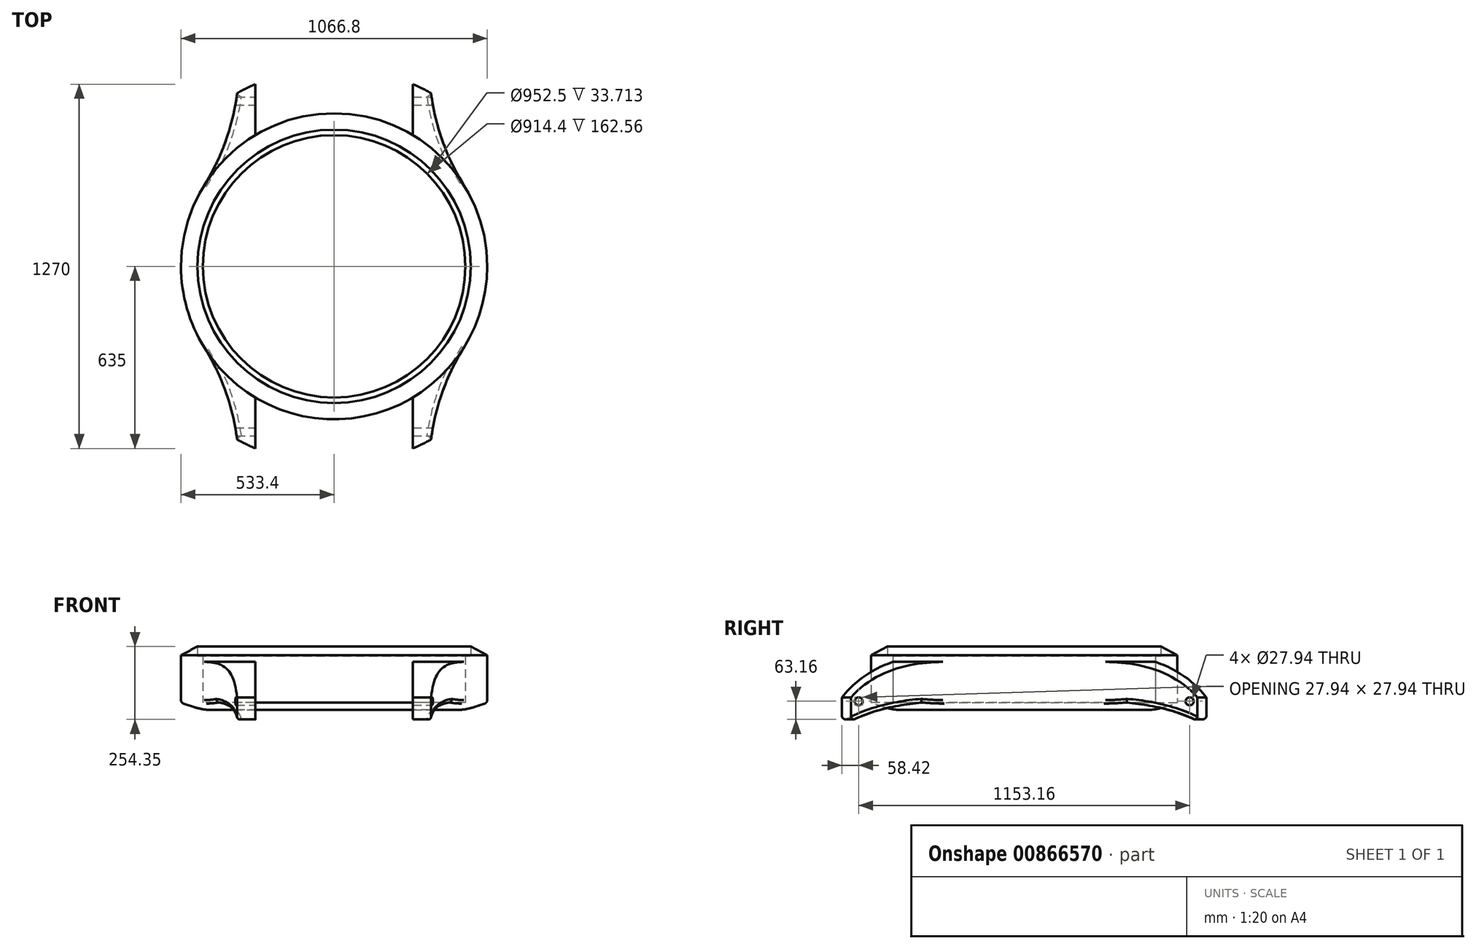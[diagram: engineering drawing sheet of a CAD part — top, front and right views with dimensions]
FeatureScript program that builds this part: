
annotation { "Feature Type Name" : "Feature", "Feature Type Description" : "" }
export const myFeature = defineFeature(function(context is Context, id is Id, definition is map)
    precondition{}
    {
        {
            var Q0;
            Q0=qCreatedBy(makeId("Top.planeOp"),FACE);
            var sketch = newSketch(context, id + "F0", { "sketchPlane" : qUnion([Q0])});
            skCircle(sketch, "E0", {"center": v(0, 0) * mm, "radius": 533.4 * mm});
            skLineSegment(sketch, "E1", {"start": v(0, 0) * mm, "end": v(533.4, 0) * mm, "construction": true});
            skLineSegment(sketch, "E2", {"start": v(0, 0) * mm, "end": v(452.35, 282.66) * mm, "construction": true});
            skLineSegment(sketch, "E3", {"start": v(452.35, 282.66) * mm, "end": v(628.97, 0) * mm, "construction": true});
            skCircle(sketch, "E4", {"center": v(0, 0) * mm, "radius": 476.25 * mm});
            skLineSegment(sketch, "E5", {"start": v(0, 0) * mm, "end": v(0, 635) * mm, "construction": true});
            skLineSegment(sketch, "E6", {"start": v(0, 635) * mm, "end": v(274.32, 635) * mm, "construction": true});
            skLineSegment(sketch, "E7", {"start": v(274.32, 635) * mm, "end": v(274.32, 457.45) * mm});
            skArc(sketch, "E8", {"start": v(337.82, 603.62) * mm, "mid": v(377.7, 436.94) * mm, "end": v(452.35, 282.66) * mm});
            skLineSegment(sketch, "E9.MirrorCS", {"start": v(-274.32, 635) * mm, "end": v(-274.32, 457.45) * mm});
            skArc(sketch, "E10.MirrorCS", {"start": v(-337.82, 603.62) * mm, "mid": v(-377.7, 436.94) * mm, "end": v(-452.35, 282.66) * mm});
            skArc(sketch, "E11.MirrorCS", {"start": v(-337.82, -603.62) * mm, "mid": v(-377.7, -436.94) * mm, "end": v(-452.35, -282.66) * mm});
            skLineSegment(sketch, "E12.MirrorCS", {"start": v(-274.32, -635) * mm, "end": v(-274.32, -457.45) * mm});
            skLineSegment(sketch, "E13.MirrorCS", {"start": v(274.32, -635) * mm, "end": v(274.32, -457.45) * mm});
            skArc(sketch, "E14.MirrorCS", {"start": v(337.82, -603.62) * mm, "mid": v(377.7, -436.94) * mm, "end": v(452.35, -282.66) * mm});
            skCircle(sketch, "E15", {"center": v(0, 0) * mm, "radius": 457.2 * mm});
            skArc(sketch, "E16", {"start": v(-337.82, -603.62) * mm, "mid": v(-306.47, -620.12) * mm, "end": v(-274.32, -635) * mm});
            skPoint(sketch, "E17.orphan", {"position": v(-331.42, 708.69) * mm});
            skPoint(sketch, "E18.MirrorCS.start.orphan", {"position": v(-274.32, 635) * mm});
            skPoint(sketch, "E19.orphan", {"position": v(331.42, 708.69) * mm});
            skPoint(sketch, "E20.MirrorCS.end.orphan", {"position": v(331.42, -708.69) * mm});
            skPoint(sketch, "E20.MirrorCS.start.orphan", {"position": v(274.32, -635) * mm});
            skPoint(sketch, "E21.orphan", {"position": v(-331.42, -708.69) * mm});
            skPoint(sketch, "E22.MirrorCS.start.orphan", {"position": v(-274.32, -635) * mm});
            skArc(sketch, "E23.trimOffspring", {"start": v(274.32, -635) * mm, "mid": v(306.47, -620.12) * mm, "end": v(337.82, -603.62) * mm});
            skArc(sketch, "E24.trimOffspring", {"start": v(337.82, 603.62) * mm, "mid": v(306.47, 620.12) * mm, "end": v(274.32, 635) * mm});
            skArc(sketch, "E25.trimOffspring", {"start": v(-274.32, 635) * mm, "mid": v(-306.47, 620.12) * mm, "end": v(-337.82, 603.62) * mm});
            skSolve(sketch);
        }
        {
            var Q0;
            Q0=qCreatedBy(makeId("Right.planeOp"),FACE);
            var sketch = newSketch(context, id + "F1", { "sketchPlane" : qUnion([Q0])});
            skLineSegment(sketch, "E26", {"start": v(0, 0) * mm, "end": v(0, -38.1) * mm});
            skLineSegment(sketch, "E27", {"start": v(-533.4, -63.5) * mm, "end": v(-723.9, -63.5) * mm});
            skLineSegment(sketch, "E28", {"start": v(-723.9, 167.64) * mm, "end": v(-723.9, -10.16) * mm});
            skLineSegment(sketch, "E29", {"start": v(-723.9, 167.64) * mm, "end": v(-533.4, 167.64) * mm});
            skArc(sketch, "E30", {"start": v(-533.4, 167.64) * mm, "mid": v(-645.52, 96.82) * mm, "end": v(-723.9, -10.16) * mm});
            skCircle(sketch, "E31", {"center": v(-576.58, 30.48) * mm, "radius": 13.97 * mm});
            skLineSegment(sketch, "E32", {"start": v(-533.4, -63.5) * mm, "end": v(-533.4, 25.4) * mm});
            skArc(sketch, "E33", {"start": v(-533.4, 25.4) * mm, "mid": v(-632.68, -10.41) * mm, "end": v(-723.9, -63.5) * mm});
            skSolve(sketch);
        }
        {
            var Q0;
            Q0=makeQuery(id+"F0.imprint","IMPRINT",FACE,{"disambiguationData":[TD([[makeQuery(id+"F0.imprint","IMPRINT",EDGE,{"derivedFrom":sQuery(id+"F0.wireOp",EDGE,"E4")}),-1.0]])]});
            extrude(context, id + "F2", {"entities" : qUnion([Q0]), "depth" : 228.6 * mm, "offsetDistance" : 25.4 * mm});
        }
        {
            var Q0;
            Q0=makeQuery(id+"F0.imprint","IMPRINT",FACE,{"disambiguationData":[TD([[makeQuery(id+"F0.imprint","IMPRINT",EDGE,{"derivedFrom":sQuery(id+"F0.wireOp",EDGE,"E4")}),1.0]])]});
            extrude(context, id + "F3", {"entities" : qUnion([Q0]), "operationType" : NewBodyOperationType.ADD, "depth" : 187.96 * mm, "offsetDistance" : 25.4 * mm});
        }
        {
            var Q0;
            {var subQ0=sQuery(id+"F0.wireOp",EDGE,"E11.MirrorCS");Q0=makeQuery(id+"F0.imprint","IMPRINT",FACE,{"disambiguationData":[TD([[makeQuery(id+"F0.imprint","IMPRINT",EDGE,{"derivedFrom":subQ0}),-1.0]])]});}
            var Q1;
            {var subQ0=sQuery(id+"F0.wireOp",EDGE,"E13.MirrorCS");Q1=makeQuery(id+"F0.imprint","IMPRINT",FACE,{"disambiguationData":[TD([[makeQuery(id+"F0.imprint","IMPRINT",EDGE,{"derivedFrom":subQ0}),-1.0]])]});}
            var Q2;
            {var subQ0=sQuery(id+"F0.wireOp",EDGE,"E9.MirrorCS");Q2=makeQuery(id+"F0.imprint","IMPRINT",FACE,{"disambiguationData":[TD([[makeQuery(id+"F0.imprint","IMPRINT",EDGE,{"derivedFrom":subQ0}),-1.0]])]});}
            var Q3;
            {var subQ0=sQuery(id+"F0.wireOp",EDGE,"E7");Q3=makeQuery(id+"F0.imprint","IMPRINT",FACE,{"disambiguationData":[TD([[makeQuery(id+"F0.imprint","IMPRINT",EDGE,{"derivedFrom":subQ0}),1.0]])]});}
            extrude(context, id + "F4", {"entities" : qUnion([Q0, Q1, Q2, Q3]), "operationType" : NewBodyOperationType.ADD, "depth" : 167.64 * mm, "hasSecondDirection" : true, "secondDirectionOppositeDirection" : true, "secondDirectionDepth" : 63.5 * mm, "offsetDistance" : 25.4 * mm});
        }
        {
            var Q0;
            Q0=makeQuery(id+"F0.imprint","IMPRINT",FACE,{"disambiguationData":[TD([[makeQuery(id+"F0.imprint","IMPRINT",EDGE,{"derivedFrom":sQuery(id+"F0.wireOp",EDGE,"E15")}),1.0]])]});
            extrude(context, id + "F5", {"entities" : qUnion([Q0]), "operationType" : NewBodyOperationType.ADD, "depth" : 25.4 * mm});
        }
        {
            var Q0;
            Q0=makeQuery(id+"F1.imprint","IMPRINT",FACE,{"disambiguationData":[TD([[makeQuery(id+"F1.imprint","IMPRINT",EDGE,{"derivedFrom":sQuery(id+"F1.wireOp",EDGE,"E28")}),1.0]])]});
            var Q1;
            Q1=makeQuery(id+"F1.imprint","IMPRINT",FACE,{"disambiguationData":[TD([[makeQuery(id+"F1.imprint","IMPRINT",EDGE,{"derivedFrom":sQuery(id+"F1.wireOp",EDGE,"E27")}),-1.0]])]});
            var Q2;
            Q2=sQuery(id+"F1.wireOp",EDGE,"E26");
            revolve(context, id + "F6", {"operationType" : NewBodyOperationType.REMOVE, "entities" : qUnion([Q0, Q1]), "axis" : qUnion([Q2]), "revolveType" : RevolveType.FULL, "oppositeDirection" : true});
        }
        {
            var Q0;
            Q0=makeQuery(id+"F1.imprint","IMPRINT",FACE,{"disambiguationData":[TD([[makeQuery(id+"F1.imprint","IMPRINT",EDGE,{"derivedFrom":sQuery(id+"F1.wireOp",EDGE,"E31")}),1.0]])]});
            extrude(context, id + "F7", {"entities" : qUnion([Q0]), "oppositeDirection" : true, "depth" : 533.4 * mm, "hasSecondDirection" : true, "secondDirectionOppositeDirection" : false, "secondDirectionDepth" : 508 * mm, "offsetDistance" : 25.4 * mm});
        }
        {
            var Q0;
            Q0=makeQuery(id+"F7.opExtrude","SWEPT_BODY",BODY,{"disambiguationData":[OSD([sQuery(id+"F1.wireOp",EDGE,"E31")])]});
            var Q1;
            Q1=qCreatedBy(makeId("Front.planeOp"),FACE);
            mirror(context, id + "F8", {"entities" : qUnion([Q0]), "mirrorPlane" : qUnion([Q1])});
        }
        {
            var Q0;
            Q0=makeQuery(id+"F7.opExtrude","SWEPT_BODY",BODY,{"disambiguationData":[OSD([sQuery(id+"F1.wireOp",EDGE,"E31")])]});
            var Q1;
            Q1=makeQuery(id+"F8.opPattern","COPY",BODY,{"derivedFrom":makeQuery(id+"F7.opExtrude","SWEPT_BODY",BODY,{"disambiguationData":[OSD([sQuery(id+"F1.wireOp",EDGE,"E31")])]}),"instanceName":"1"});
            var Q2;
            Q2=makeQuery(id+"F2.opExtrude","SWEPT_BODY",BODY,{"disambiguationData":[OSD([sQuery(id+"F0.wireOp",EDGE,"E0"),sQuery(id+"F0.wireOp",EDGE,"E4")])]});
            booleanBodies(context, id + "F9", {"operationType" : BooleanOperationType.SUBTRACTION, "tools" : qUnion([Q0, Q1]), "targets" : qUnion([Q2])});
        }
        {
            var Q0;
            Q0=makeQuery(id+"F2.opExtrude","CAP_EDGE",EDGE,{"disambiguationData":[OSD([sQuery(id+"F0.wireOp",EDGE,"E0")])],"isStart":false});
            chamfer(context, id + "F10", {"entities" : qUnion([Q0]), "chamferType" : ChamferType.TWO_OFFSETS, "width1" : 69.85 * mm, "oppositeDirection" : false, "width2" : 38.1 * mm, "tangentPropagation" : true});
        }
        {
            var Q0;
            {var subQ0=sQuery(id+"F0.wireOp",EDGE,"E15");var subQ1=sQuery(id+"F0.wireOp",EDGE,"3gFhJr65-xv2Y-erHj-zoJU-6mu3HS65LAeQ");var subQ2=makeQuery(id+"FME4PPcdAdgup70_1.opExtrude","CAP_FACE",FACE,{"disambiguationData":[OSD([subQ1,subQ0])],"isStart":true});var subQ3=sQuery(id+"F0.wireOp",EDGE,"E4");var subQ4=makeQuery(id+"F3.opExtrude","CAP_FACE",FACE,{"disambiguationData":[OSD([subQ3,subQ0])],"isStart":true});var subQ5=sQuery(id+"F0.wireOp",EDGE,"E13.MirrorCS");var subQ6=sQuery(id+"F0.wireOp",EDGE,"E0");var subQ7=makeQuery(id+"F2.opExtrude","CAP_FACE",FACE,{"disambiguationData":[OSD([subQ6,subQ3])],"isStart":true});var subQ8=sQuery(id+"F0.wireOp",EDGE,"E11.MirrorCS");var subQ9=sQuery(id+"F0.wireOp",EDGE,"E12.MirrorCS");var subQ10=makeQuery(id+"F4.opExtrude","SWEPT_FACE",FACE,{"disambiguationData":[OSD([subQ6]),TDD([makeQuery(id+"F0.imprint","IMPRINT",EDGE,{"disambiguationData":[TD([[makeQuery(id+"F0.imprint","INTERSECT",VERTEX,{"derivedFrom":[subQ6,subQ8]}),-1.0]])],"derivedFrom":subQ6})])]});var subQ11=makeQuery(id+"F2.opExtrude","SWEPT_FACE",FACE,{"disambiguationData":[OSD([subQ6])]});var subQ12=makeQuery(id+"FiIen0mHaqCyIIV_1.opExtrude","CAP_FACE",FACE,{"disambiguationData":[OSD([subQ1])],"isStart":true});var subQ14=makeQuery(id+"F4.opExtrude","SWEPT_FACE",FACE,{"disambiguationData":[OSD([subQ6]),TDD([makeQuery(id+"F0.imprint","IMPRINT",EDGE,{"disambiguationData":[TD([[makeQuery(id+"F0.imprint","INTERSECT",VERTEX,{"derivedFrom":[subQ6,subQ5]}),-1.0]])],"derivedFrom":subQ6})])]});var subQ15=makeQuery(id+"F2.opExtrude","CAP_EDGE",EDGE,{"disambiguationData":[OSD([subQ6])],"isStart":true});var subQ16=sQuery(id+"F0.wireOp",EDGE,"E10.MirrorCS");var subQ17=sQuery(id+"F0.wireOp",EDGE,"E9.MirrorCS");var subQ18=makeQuery(id+"F4.opExtrude","SWEPT_FACE",FACE,{"disambiguationData":[OSD([subQ6]),TDD([makeQuery(id+"F0.imprint","IMPRINT",EDGE,{"disambiguationData":[TD([[makeQuery(id+"F0.imprint","INTERSECT",VERTEX,{"derivedFrom":[subQ6,subQ17]}),-1.0]])],"derivedFrom":subQ6})])]});var subQ19=sQuery(id+"F0.wireOp",EDGE,"E7");var subQ20=sQuery(id+"F0.wireOp",EDGE,"E8");var subQ21=makeQuery(id+"F4.opExtrude","SWEPT_FACE",FACE,{"disambiguationData":[OSD([subQ6]),TDD([makeQuery(id+"F0.imprint","IMPRINT",EDGE,{"disambiguationData":[TD([[makeQuery(id+"F0.imprint","INTERSECT",VERTEX,{"derivedFrom":[subQ6,subQ19]}),1.0]])],"derivedFrom":subQ6})])]});Q0=makeQuery(id+"F6.boolean.opBoolean","MERGE",EDGE,{"derivedFrom":[makeQuery(id+"F4.boolean.opBoolean","SPLIT",EDGE,{"disambiguationData":[topologyDisambiguationEdgeConnected([subQ7,subQ4,subQ2,subQ12,subQ21])],"derivedFrom":subQ15}),makeQuery(id+"F4.boolean.opBoolean","SPLIT",EDGE,{"disambiguationData":[topologyDisambiguationEdgeConnected([subQ7,subQ4,subQ2,subQ12,subQ18])],"derivedFrom":subQ15}),makeQuery(id+"F4.boolean.opBoolean","SPLIT",EDGE,{"disambiguationData":[topologyDisambiguationEdgeConnected([subQ7,subQ4,subQ2,subQ12,subQ10])],"derivedFrom":subQ15}),makeQuery(id+"F4.boolean.opBoolean","SPLIT",EDGE,{"disambiguationData":[topologyDisambiguationEdgeConnected([subQ7,subQ4,subQ2,subQ12,subQ14])],"derivedFrom":subQ15}),makeQuery(id+"F4.boolean.opBoolean","SPLIT",EDGE,{"disambiguationData":[topologyDisambiguationEdgeConnected([subQ11,subQ7,subQ4,subQ2,subQ12]),TD([makeQuery(id+"F4.opExtrude","SWEPT_FACE",FACE,{"disambiguationData":[OSD([subQ19])]})])],"derivedFrom":subQ15}),makeQuery(id+"F4.boolean.opBoolean","SPLIT",EDGE,{"disambiguationData":[topologyDisambiguationEdgeConnected([subQ11,subQ7,subQ4,subQ2,subQ12]),TD([makeQuery(id+"F4.opExtrude","SWEPT_FACE",FACE,{"disambiguationData":[OSD([subQ20])]})])],"derivedFrom":subQ15}),makeQuery(id+"F4.boolean.opBoolean","SPLIT",EDGE,{"disambiguationData":[topologyDisambiguationEdgeConnected([subQ11,subQ7,subQ4,subQ2,subQ12]),TD([makeQuery(id+"F4.opExtrude","SWEPT_FACE",FACE,{"disambiguationData":[OSD([subQ16])]})])],"derivedFrom":subQ15}),makeQuery(id+"F4.boolean.opBoolean","SPLIT",EDGE,{"disambiguationData":[topologyDisambiguationEdgeConnected([subQ11,subQ7,subQ4,subQ2,subQ12]),TD([makeQuery(id+"F4.opExtrude","SWEPT_FACE",FACE,{"disambiguationData":[OSD([subQ9])]})])],"derivedFrom":subQ15})]});}
            chamfer(context, id + "F11", {"entities" : qUnion([Q0]), "chamferType" : ChamferType.TWO_OFFSETS, "width1" : 25.4 * mm, "oppositeDirection" : false, "width2" : 76.2 * mm, "tangentPropagation" : true});
        }
        {
            var Q0;
            {var subQ0=sQuery(id+"F0.wireOp",EDGE,"3gFhJr65-xv2Y-erHj-zoJU-6mu3HS65LAeQ");var subQ1=makeQuery(id+"FiIen0mHaqCyIIV_1.opExtrude","CAP_FACE",FACE,{"disambiguationData":[OSD([subQ0])],"isStart":true});var subQ2=sQuery(id+"F0.wireOp",EDGE,"E15");var subQ3=makeQuery(id+"FME4PPcdAdgup70_1.opExtrude","CAP_FACE",FACE,{"disambiguationData":[OSD([subQ0,subQ2])],"isStart":true});var subQ4=sQuery(id+"F0.wireOp",EDGE,"E4");var subQ5=makeQuery(id+"F3.opExtrude","CAP_FACE",FACE,{"disambiguationData":[OSD([subQ4,subQ2])],"isStart":true});var subQ6=sQuery(id+"F0.wireOp",EDGE,"E0");var subQ7=makeQuery(id+"F2.opExtrude","CAP_FACE",FACE,{"disambiguationData":[OSD([subQ6,subQ4])],"isStart":true});var subQ8=sQuery(id+"F0.wireOp",EDGE,"E13.MirrorCS");var subQ9=sQuery(id+"F0.wireOp",EDGE,"E11.MirrorCS");var subQ10=sQuery(id+"F0.wireOp",EDGE,"E12.MirrorCS");var subQ11=makeQuery(id+"F4.opExtrude","SWEPT_FACE",FACE,{"disambiguationData":[OSD([subQ6]),TDD([makeQuery(id+"F0.imprint","IMPRINT",EDGE,{"disambiguationData":[TD([[makeQuery(id+"F0.imprint","INTERSECT",VERTEX,{"derivedFrom":[subQ6,subQ9]}),-1.0]])],"derivedFrom":subQ6})])]});var subQ12=makeQuery(id+"F2.opExtrude","SWEPT_FACE",FACE,{"disambiguationData":[OSD([subQ6])]});var subQ14=makeQuery(id+"F4.opExtrude","SWEPT_FACE",FACE,{"disambiguationData":[OSD([subQ6]),TDD([makeQuery(id+"F0.imprint","IMPRINT",EDGE,{"disambiguationData":[TD([[makeQuery(id+"F0.imprint","INTERSECT",VERTEX,{"derivedFrom":[subQ6,subQ8]}),-1.0]])],"derivedFrom":subQ6})])]});var subQ15=makeQuery(id+"F2.opExtrude","CAP_EDGE",EDGE,{"disambiguationData":[OSD([subQ6])],"isStart":true});var subQ16=sQuery(id+"F0.wireOp",EDGE,"E10.MirrorCS");var subQ17=sQuery(id+"F0.wireOp",EDGE,"E9.MirrorCS");var subQ18=makeQuery(id+"F4.opExtrude","SWEPT_FACE",FACE,{"disambiguationData":[OSD([subQ6]),TDD([makeQuery(id+"F0.imprint","IMPRINT",EDGE,{"disambiguationData":[TD([[makeQuery(id+"F0.imprint","INTERSECT",VERTEX,{"derivedFrom":[subQ6,subQ17]}),-1.0]])],"derivedFrom":subQ6})])]});var subQ19=sQuery(id+"F0.wireOp",EDGE,"E7");var subQ20=sQuery(id+"F0.wireOp",EDGE,"E8");var subQ21=makeQuery(id+"F4.opExtrude","SWEPT_FACE",FACE,{"disambiguationData":[OSD([subQ6]),TDD([makeQuery(id+"F0.imprint","IMPRINT",EDGE,{"disambiguationData":[TD([[makeQuery(id+"F0.imprint","INTERSECT",VERTEX,{"derivedFrom":[subQ6,subQ19]}),1.0]])],"derivedFrom":subQ6})])]});Q0=makeQuery(id+"F11.opChamfer","BLEND_EDGE",EDGE,{"blendedFrom":[makeQuery(id+"F6.boolean.opBoolean","MERGE",EDGE,{"derivedFrom":[makeQuery(id+"F4.boolean.opBoolean","SPLIT",EDGE,{"disambiguationData":[topologyDisambiguationEdgeConnected([subQ7,subQ5,subQ3,subQ1,subQ21])],"derivedFrom":subQ15}),makeQuery(id+"F4.boolean.opBoolean","SPLIT",EDGE,{"disambiguationData":[topologyDisambiguationEdgeConnected([subQ7,subQ5,subQ3,subQ1,subQ18])],"derivedFrom":subQ15}),makeQuery(id+"F4.boolean.opBoolean","SPLIT",EDGE,{"disambiguationData":[topologyDisambiguationEdgeConnected([subQ7,subQ5,subQ3,subQ1,subQ11])],"derivedFrom":subQ15}),makeQuery(id+"F4.boolean.opBoolean","SPLIT",EDGE,{"disambiguationData":[topologyDisambiguationEdgeConnected([subQ7,subQ5,subQ3,subQ1,subQ14])],"derivedFrom":subQ15}),makeQuery(id+"F4.boolean.opBoolean","SPLIT",EDGE,{"disambiguationData":[topologyDisambiguationEdgeConnected([subQ12,subQ7,subQ5,subQ3,subQ1]),TD([makeQuery(id+"F4.opExtrude","SWEPT_FACE",FACE,{"disambiguationData":[OSD([subQ19])]})])],"derivedFrom":subQ15}),makeQuery(id+"F4.boolean.opBoolean","SPLIT",EDGE,{"disambiguationData":[topologyDisambiguationEdgeConnected([subQ12,subQ7,subQ5,subQ3,subQ1]),TD([makeQuery(id+"F4.opExtrude","SWEPT_FACE",FACE,{"disambiguationData":[OSD([subQ20])]})])],"derivedFrom":subQ15}),makeQuery(id+"F4.boolean.opBoolean","SPLIT",EDGE,{"disambiguationData":[topologyDisambiguationEdgeConnected([subQ12,subQ7,subQ5,subQ3,subQ1]),TD([makeQuery(id+"F4.opExtrude","SWEPT_FACE",FACE,{"disambiguationData":[OSD([subQ16])]})])],"derivedFrom":subQ15}),makeQuery(id+"F4.boolean.opBoolean","SPLIT",EDGE,{"disambiguationData":[topologyDisambiguationEdgeConnected([subQ12,subQ7,subQ5,subQ3,subQ1]),TD([makeQuery(id+"F4.opExtrude","SWEPT_FACE",FACE,{"disambiguationData":[OSD([subQ10])]})])],"derivedFrom":subQ15})]}),makeQuery(id+"FiIen0mHaqCyIIV_1.boolean.opBoolean","MERGE",FACE,{"derivedFrom":[makeQuery(id+"FME4PPcdAdgup70_1.boolean.opBoolean","MERGE",FACE,{"derivedFrom":[makeQuery(id+"F3.boolean.opBoolean","MERGE",FACE,{"derivedFrom":[subQ7,subQ5]}),subQ3]}),subQ1]})],"blendedInto":[makeQuery(id+"FiIen0mHaqCyIIV_1.boolean.opBoolean","MERGE",FACE,{"derivedFrom":[makeQuery(id+"FME4PPcdAdgup70_1.boolean.opBoolean","MERGE",FACE,{"derivedFrom":[makeQuery(id+"F3.boolean.opBoolean","MERGE",FACE,{"derivedFrom":[subQ7,subQ5]}),subQ3]}),subQ1]})]});}
            fillet(context, id + "F12", {"entities" : qUnion([Q0]), "radius" : 203.2 * mm, "tangentPropagation" : true, "allowEdgeOverflow" : false});
        }
        {
            var Q0;
            Q0=makeQuery(id+"F6.boolean.opBoolean","INTERSECT",EDGE,{"derivedFrom":[makeQuery(id+"F4.opExtrude","SWEPT_FACE",FACE,{"disambiguationData":[OSD([sQuery(id+"F0.wireOp",EDGE,"E10.MirrorCS")])]}),makeQuery(id+"F6.opRevolve","SWEPT_FACE",FACE,{"disambiguationData":[OSD([sQuery(id+"F1.wireOp",EDGE,"E33")])]})]});
            var Q1;
            Q1=makeQuery(id+"F6.boolean.opBoolean","INTERSECT",EDGE,{"derivedFrom":[makeQuery(id+"F4.opExtrude","SWEPT_FACE",FACE,{"disambiguationData":[OSD([sQuery(id+"F0.wireOp",EDGE,"E25.trimOffspring")])]}),makeQuery(id+"F6.opRevolve","SWEPT_FACE",FACE,{"disambiguationData":[OSD([sQuery(id+"F1.wireOp",EDGE,"E33")])]})]});
            var Q2;
            Q2=makeQuery(id+"F6.boolean.opBoolean","INTERSECT",EDGE,{"derivedFrom":[makeQuery(id+"F4.opExtrude","SWEPT_FACE",FACE,{"disambiguationData":[OSD([sQuery(id+"F0.wireOp",EDGE,"E8")])]}),makeQuery(id+"F6.opRevolve","SWEPT_FACE",FACE,{"disambiguationData":[OSD([sQuery(id+"F1.wireOp",EDGE,"E33")])]})]});
            var Q3;
            Q3=makeQuery(id+"F6.boolean.opBoolean","INTERSECT",EDGE,{"derivedFrom":[makeQuery(id+"F4.opExtrude","SWEPT_FACE",FACE,{"disambiguationData":[OSD([sQuery(id+"F0.wireOp",EDGE,"E24.trimOffspring")])]}),makeQuery(id+"F6.opRevolve","SWEPT_FACE",FACE,{"disambiguationData":[OSD([sQuery(id+"F1.wireOp",EDGE,"E33")])]})]});
            var Q4;
            Q4=makeQuery(id+"F6.boolean.opBoolean","INTERSECT",EDGE,{"derivedFrom":[makeQuery(id+"F4.opExtrude","SWEPT_FACE",FACE,{"disambiguationData":[OSD([sQuery(id+"F0.wireOp",EDGE,"E11.MirrorCS")])]}),makeQuery(id+"F6.opRevolve","SWEPT_FACE",FACE,{"disambiguationData":[OSD([sQuery(id+"F1.wireOp",EDGE,"E33")])]})]});
            var Q5;
            Q5=makeQuery(id+"F6.boolean.opBoolean","INTERSECT",EDGE,{"derivedFrom":[makeQuery(id+"F4.opExtrude","SWEPT_FACE",FACE,{"disambiguationData":[OSD([sQuery(id+"F0.wireOp",EDGE,"E16")])]}),makeQuery(id+"F6.opRevolve","SWEPT_FACE",FACE,{"disambiguationData":[OSD([sQuery(id+"F1.wireOp",EDGE,"E33")])]})]});
            var Q6;
            Q6=makeQuery(id+"F6.boolean.opBoolean","INTERSECT",EDGE,{"derivedFrom":[makeQuery(id+"F4.opExtrude","SWEPT_FACE",FACE,{"disambiguationData":[OSD([sQuery(id+"F0.wireOp",EDGE,"E14.MirrorCS")])]}),makeQuery(id+"F6.opRevolve","SWEPT_FACE",FACE,{"disambiguationData":[OSD([sQuery(id+"F1.wireOp",EDGE,"E33")])]})]});
            var Q7;
            Q7=makeQuery(id+"F6.boolean.opBoolean","INTERSECT",EDGE,{"derivedFrom":[makeQuery(id+"F4.opExtrude","SWEPT_FACE",FACE,{"disambiguationData":[OSD([sQuery(id+"F0.wireOp",EDGE,"E23.trimOffspring")])]}),makeQuery(id+"F6.opRevolve","SWEPT_FACE",FACE,{"disambiguationData":[OSD([sQuery(id+"F1.wireOp",EDGE,"E33")])]})]});
            fillet(context, id + "F13", {"entities" : qUnion([Q0, Q1, Q2, Q3, Q4, Q5, Q6, Q7]), "radius" : 12.7 * mm, "tangentPropagation" : true, "allowEdgeOverflow" : false});
        }
    });
